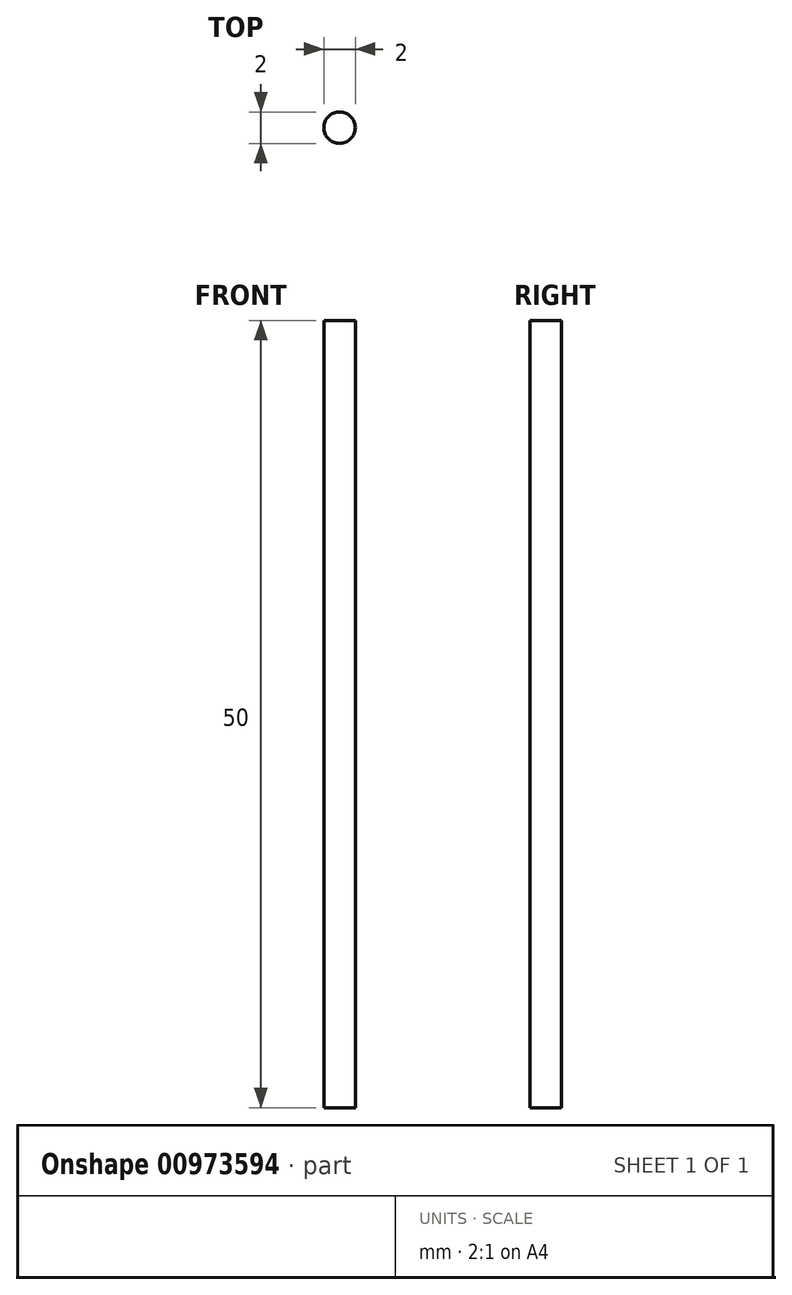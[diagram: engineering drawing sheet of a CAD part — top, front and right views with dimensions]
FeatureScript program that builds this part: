
annotation { "Feature Type Name" : "Feature", "Feature Type Description" : "" }
export const myFeature = defineFeature(function(context is Context, id is Id, definition is map)
    precondition{}
    {
        {
            var Q0;
            Q0=qCreatedBy(makeId("Top.planeOp"),FACE);
            var sketch = newSketch(context, id + "F0", { "sketchPlane" : qUnion([Q0])});
            skCircle(sketch, "E0", {"center": v(0, 0) * mm, "radius": 1 * mm});
            skSolve(sketch);
        }
        {
            var Q0;
            Q0 = qSketchRegion(id + "F0", true);
            extrude(context, id + "F1", {"entities" : qUnion([Q0]), "depth" : 50 * mm, "offsetDistance" : 25 * mm});
        }
    });
